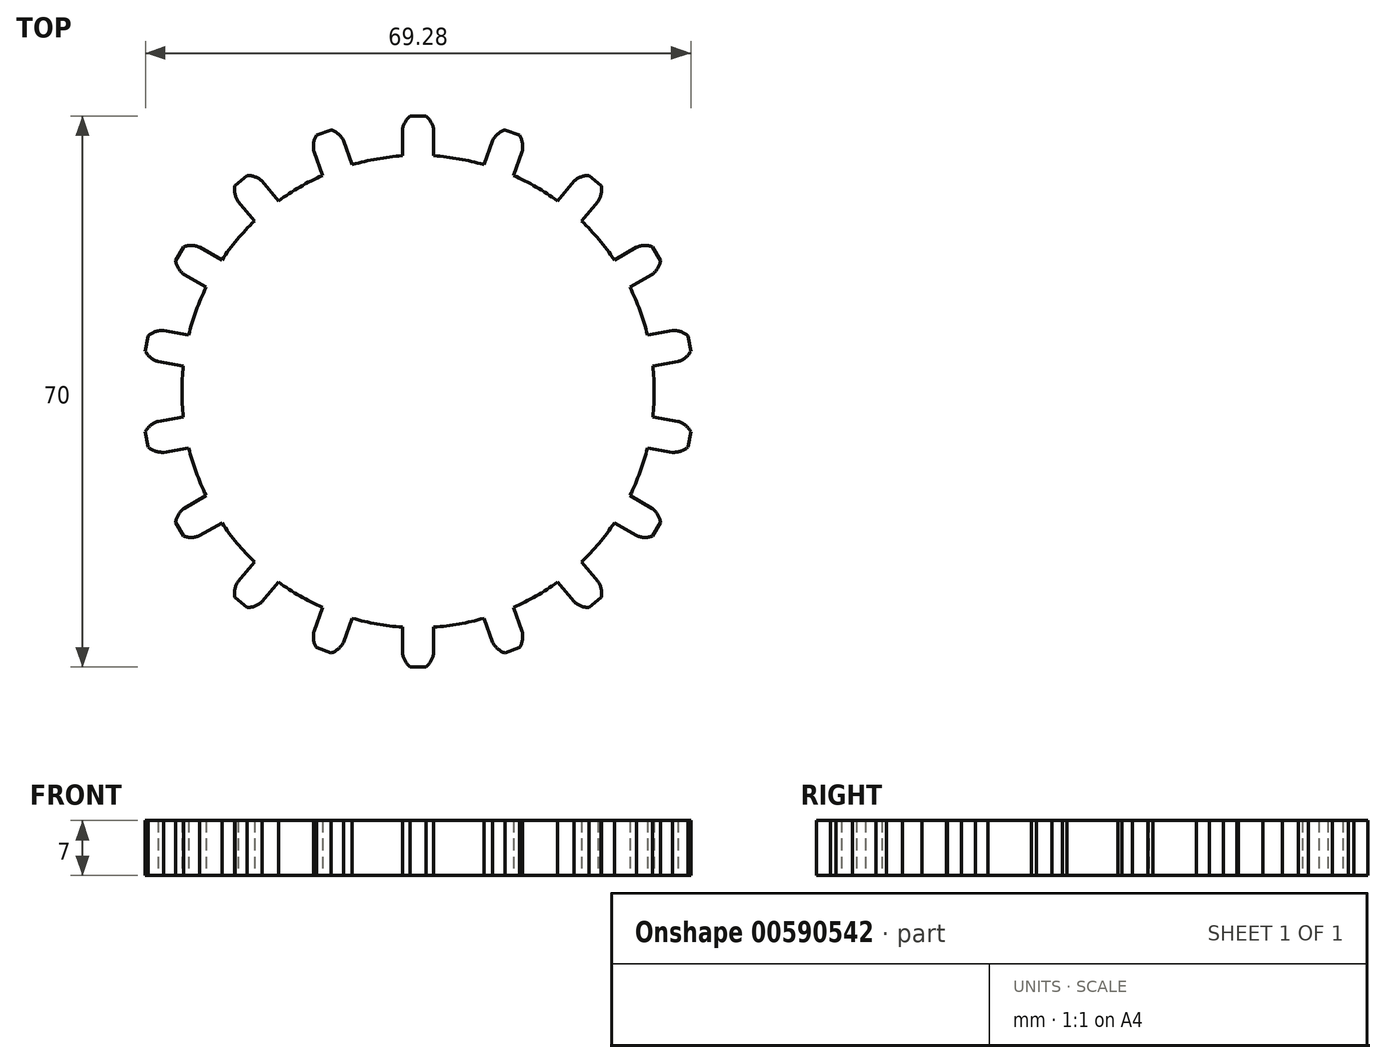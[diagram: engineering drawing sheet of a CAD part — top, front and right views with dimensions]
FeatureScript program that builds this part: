
annotation { "Feature Type Name" : "Feature", "Feature Type Description" : "" }
export const myFeature = defineFeature(function(context is Context, id is Id, definition is map)
    precondition{}
    {
        {
            var Q0;
            Q0=qCreatedBy(makeId("Top.planeOp"),FACE);
            var sketch = newSketch(context, id + "F0", { "sketchPlane" : qUnion([Q0])});
            skCircle(sketch, "E0", {"center": v(0, 0) * mm, "radius": 30 * mm});
            skLineSegment(sketch, "E1", {"start": v(0, 35) * mm, "end": v(1, 35) * mm});
            skLineSegment(sketch, "E2", {"start": v(2, 33.18) * mm, "end": v(2, 29.93) * mm});
            skPoint(sketch, "E3", {"position": v(1, 35) * mm});
            skArc(sketch, "E4", {"start": v(2, 32.47) * mm, "mid": v(1.82, 33.86) * mm, "end": v(1, 35) * mm});
            skPoint(sketch, "E5.MirrorCS.start.orphan", {"position": v(0, 35) * mm});
            skArc(sketch, "E6.MirrorCS", {"start": v(-2, 32.47) * mm, "mid": v(-1.82, 33.86) * mm, "end": v(-1, 35) * mm});
            skLineSegment(sketch, "E7.MirrorCS", {"start": v(-2, 33.18) * mm, "end": v(-2, 29.93) * mm});
            skLineSegment(sketch, "E8.MirrorCS", {"start": v(0, 35) * mm, "end": v(-1, 35) * mm});
            skLineSegment(sketch, "E9.1.0", {"start": v(-13.23, 30.5) * mm, "end": v(-12.12, 27.44) * mm});
            skLineSegment(sketch, "E9.1.1", {"start": v(-9.47, 31.86) * mm, "end": v(-8.36, 28.81) * mm});
            skPoint(sketch, "E9.1.2", {"position": v(-11.97, 32.89) * mm});
            skPoint(sketch, "E9.1.3", {"position": v(-11.03, 33.23) * mm});
            skArc(sketch, "E9.1.4", {"start": v(-12.98, 29.82) * mm, "mid": v(-13.3, 31.2) * mm, "end": v(-12.91, 32.55) * mm});
            skArc(sketch, "E9.1.5", {"start": v(-9.22, 31.2) * mm, "mid": v(-9.87, 32.44) * mm, "end": v(-11.03, 33.23) * mm});
            skLineSegment(sketch, "E9.1.6", {"start": v(-11.97, 32.89) * mm, "end": v(-12.91, 32.55) * mm});
            skLineSegment(sketch, "E9.1.7", {"start": v(-11.97, 32.89) * mm, "end": v(-11.03, 33.23) * mm});
            skLineSegment(sketch, "E9.2.0", {"start": v(-22.86, 24.13) * mm, "end": v(-20.77, 21.64) * mm});
            skLineSegment(sketch, "E9.2.1", {"start": v(-19.8, 26.7) * mm, "end": v(-17.7, 24.22) * mm});
            skPoint(sketch, "E9.2.2", {"position": v(-22.5, 26.81) * mm});
            skPoint(sketch, "E9.2.3", {"position": v(-21.73, 27.45) * mm});
            skArc(sketch, "E9.2.4", {"start": v(-22.4, 23.59) * mm, "mid": v(-23.16, 24.77) * mm, "end": v(-23.26, 26.17) * mm});
            skArc(sketch, "E9.2.5", {"start": v(-19.34, 26.16) * mm, "mid": v(-20.37, 27.11) * mm, "end": v(-21.73, 27.45) * mm});
            skLineSegment(sketch, "E9.2.6", {"start": v(-22.5, 26.81) * mm, "end": v(-23.26, 26.17) * mm});
            skLineSegment(sketch, "E9.2.7", {"start": v(-22.5, 26.81) * mm, "end": v(-21.73, 27.45) * mm});
            skLineSegment(sketch, "E9.3.0", {"start": v(-29.73, 14.86) * mm, "end": v(-26.92, 13.23) * mm});
            skLineSegment(sketch, "E9.3.1", {"start": v(-27.73, 18.32) * mm, "end": v(-24.92, 16.7) * mm});
            skPoint(sketch, "E9.3.2", {"position": v(-30.31, 17.5) * mm});
            skPoint(sketch, "E9.3.3", {"position": v(-29.81, 18.37) * mm});
            skArc(sketch, "E9.3.4", {"start": v(-29.12, 14.5) * mm, "mid": v(-30.24, 15.35) * mm, "end": v(-30.81, 16.63) * mm});
            skArc(sketch, "E9.3.5", {"start": v(-27.12, 17.97) * mm, "mid": v(-28.41, 18.51) * mm, "end": v(-29.81, 18.37) * mm});
            skLineSegment(sketch, "E9.3.6", {"start": v(-30.31, 17.5) * mm, "end": v(-30.81, 16.63) * mm});
            skLineSegment(sketch, "E9.3.7", {"start": v(-30.31, 17.5) * mm, "end": v(-29.81, 18.37) * mm});
            skLineSegment(sketch, "E9.4.0", {"start": v(-33.02, 3.8) * mm, "end": v(-29.83, 3.23) * mm});
            skLineSegment(sketch, "E9.4.1", {"start": v(-32.32, 7.73) * mm, "end": v(-29.13, 7.17) * mm});
            skPoint(sketch, "E9.4.2", {"position": v(-34.47, 6.08) * mm});
            skPoint(sketch, "E9.4.3", {"position": v(-34.3, 7.06) * mm});
            skArc(sketch, "E9.4.4", {"start": v(-32.32, 3.67) * mm, "mid": v(-33.66, 4.08) * mm, "end": v(-34.64, 5.1) * mm});
            skArc(sketch, "E9.4.5", {"start": v(-31.63, 7.6) * mm, "mid": v(-33.03, 7.68) * mm, "end": v(-34.3, 7.06) * mm});
            skLineSegment(sketch, "E9.4.6", {"start": v(-34.47, 6.08) * mm, "end": v(-34.64, 5.1) * mm});
            skLineSegment(sketch, "E9.4.7", {"start": v(-34.47, 6.08) * mm, "end": v(-34.3, 7.06) * mm});
            skLineSegment(sketch, "E9.5.0", {"start": v(-32.32, -7.73) * mm, "end": v(-29.13, -7.17) * mm});
            skLineSegment(sketch, "E9.5.1", {"start": v(-33.02, -3.8) * mm, "end": v(-29.83, -3.23) * mm});
            skPoint(sketch, "E9.5.2", {"position": v(-34.47, -6.08) * mm});
            skPoint(sketch, "E9.5.3", {"position": v(-34.64, -5.1) * mm});
            skArc(sketch, "E9.5.4", {"start": v(-31.63, -7.6) * mm, "mid": v(-33.03, -7.68) * mm, "end": v(-34.3, -7.06) * mm});
            skArc(sketch, "E9.5.5", {"start": v(-32.32, -3.67) * mm, "mid": v(-33.66, -4.08) * mm, "end": v(-34.64, -5.1) * mm});
            skLineSegment(sketch, "E9.5.6", {"start": v(-34.47, -6.08) * mm, "end": v(-34.3, -7.06) * mm});
            skLineSegment(sketch, "E9.5.7", {"start": v(-34.47, -6.08) * mm, "end": v(-34.64, -5.1) * mm});
            skLineSegment(sketch, "E9.6.0", {"start": v(-27.73, -18.32) * mm, "end": v(-24.92, -16.7) * mm});
            skLineSegment(sketch, "E9.6.1", {"start": v(-29.73, -14.86) * mm, "end": v(-26.92, -13.23) * mm});
            skPoint(sketch, "E9.6.2", {"position": v(-30.31, -17.5) * mm});
            skPoint(sketch, "E9.6.3", {"position": v(-30.81, -16.63) * mm});
            skArc(sketch, "E9.6.4", {"start": v(-27.12, -17.97) * mm, "mid": v(-28.41, -18.51) * mm, "end": v(-29.81, -18.37) * mm});
            skArc(sketch, "E9.6.5", {"start": v(-29.12, -14.5) * mm, "mid": v(-30.24, -15.35) * mm, "end": v(-30.81, -16.63) * mm});
            skLineSegment(sketch, "E9.6.6", {"start": v(-30.31, -17.5) * mm, "end": v(-29.81, -18.37) * mm});
            skLineSegment(sketch, "E9.6.7", {"start": v(-30.31, -17.5) * mm, "end": v(-30.81, -16.63) * mm});
            skLineSegment(sketch, "E9.7.0", {"start": v(-19.8, -26.7) * mm, "end": v(-17.7, -24.22) * mm});
            skLineSegment(sketch, "E9.7.1", {"start": v(-22.86, -24.13) * mm, "end": v(-20.77, -21.64) * mm});
            skPoint(sketch, "E9.7.2", {"position": v(-22.5, -26.81) * mm});
            skPoint(sketch, "E9.7.3", {"position": v(-23.26, -26.17) * mm});
            skArc(sketch, "E9.7.4", {"start": v(-19.34, -26.16) * mm, "mid": v(-20.37, -27.11) * mm, "end": v(-21.73, -27.45) * mm});
            skArc(sketch, "E9.7.5", {"start": v(-22.4, -23.59) * mm, "mid": v(-23.16, -24.77) * mm, "end": v(-23.26, -26.17) * mm});
            skLineSegment(sketch, "E9.7.6", {"start": v(-22.5, -26.81) * mm, "end": v(-21.73, -27.45) * mm});
            skLineSegment(sketch, "E9.7.7", {"start": v(-22.5, -26.81) * mm, "end": v(-23.26, -26.17) * mm});
            skLineSegment(sketch, "E9.8.0", {"start": v(-9.47, -31.86) * mm, "end": v(-8.36, -28.81) * mm});
            skLineSegment(sketch, "E9.8.1", {"start": v(-13.23, -30.5) * mm, "end": v(-12.12, -27.44) * mm});
            skPoint(sketch, "E9.8.2", {"position": v(-11.97, -32.89) * mm});
            skPoint(sketch, "E9.8.3", {"position": v(-12.91, -32.55) * mm});
            skArc(sketch, "E9.8.4", {"start": v(-9.22, -31.2) * mm, "mid": v(-9.87, -32.44) * mm, "end": v(-11.03, -33.23) * mm});
            skArc(sketch, "E9.8.5", {"start": v(-12.98, -29.82) * mm, "mid": v(-13.3, -31.2) * mm, "end": v(-12.91, -32.55) * mm});
            skLineSegment(sketch, "E9.8.6", {"start": v(-11.97, -32.89) * mm, "end": v(-11.03, -33.23) * mm});
            skLineSegment(sketch, "E9.8.7", {"start": v(-11.97, -32.89) * mm, "end": v(-12.91, -32.55) * mm});
            skLineSegment(sketch, "E9.9.0", {"start": v(2, -33.18) * mm, "end": v(2, -29.93) * mm});
            skLineSegment(sketch, "E9.9.1", {"start": v(-2, -33.18) * mm, "end": v(-2, -29.93) * mm});
            skPoint(sketch, "E9.9.2", {"position": v(0, -35) * mm});
            skPoint(sketch, "E9.9.3", {"position": v(-1, -35) * mm});
            skArc(sketch, "E9.9.4", {"start": v(2, -32.47) * mm, "mid": v(1.82, -33.86) * mm, "end": v(1, -35) * mm});
            skArc(sketch, "E9.9.5", {"start": v(-2, -32.47) * mm, "mid": v(-1.82, -33.86) * mm, "end": v(-1, -35) * mm});
            skLineSegment(sketch, "E9.9.6", {"start": v(0, -35) * mm, "end": v(1, -35) * mm});
            skLineSegment(sketch, "E9.9.7", {"start": v(0, -35) * mm, "end": v(-1, -35) * mm});
            skLineSegment(sketch, "E9.10.0", {"start": v(13.23, -30.5) * mm, "end": v(12.12, -27.44) * mm});
            skLineSegment(sketch, "E9.10.1", {"start": v(9.47, -31.86) * mm, "end": v(8.36, -28.81) * mm});
            skPoint(sketch, "E9.10.2", {"position": v(11.97, -32.89) * mm});
            skPoint(sketch, "E9.10.3", {"position": v(11.03, -33.23) * mm});
            skArc(sketch, "E9.10.4", {"start": v(12.98, -29.82) * mm, "mid": v(13.3, -31.2) * mm, "end": v(12.91, -32.55) * mm});
            skArc(sketch, "E9.10.5", {"start": v(9.22, -31.2) * mm, "mid": v(9.87, -32.44) * mm, "end": v(11.03, -33.23) * mm});
            skLineSegment(sketch, "E9.10.6", {"start": v(11.97, -32.89) * mm, "end": v(12.91, -32.55) * mm});
            skLineSegment(sketch, "E9.10.7", {"start": v(11.97, -32.89) * mm, "end": v(11.03, -33.23) * mm});
            skLineSegment(sketch, "E9.11.0", {"start": v(22.86, -24.13) * mm, "end": v(20.77, -21.64) * mm});
            skLineSegment(sketch, "E9.11.1", {"start": v(19.8, -26.7) * mm, "end": v(17.7, -24.22) * mm});
            skPoint(sketch, "E9.11.2", {"position": v(22.5, -26.81) * mm});
            skPoint(sketch, "E9.11.3", {"position": v(21.73, -27.45) * mm});
            skArc(sketch, "E9.11.4", {"start": v(22.4, -23.59) * mm, "mid": v(23.16, -24.77) * mm, "end": v(23.26, -26.17) * mm});
            skArc(sketch, "E9.11.5", {"start": v(19.34, -26.16) * mm, "mid": v(20.37, -27.11) * mm, "end": v(21.73, -27.45) * mm});
            skLineSegment(sketch, "E9.11.6", {"start": v(22.5, -26.81) * mm, "end": v(23.26, -26.17) * mm});
            skLineSegment(sketch, "E9.11.7", {"start": v(22.5, -26.81) * mm, "end": v(21.73, -27.45) * mm});
            skLineSegment(sketch, "E9.12.0", {"start": v(29.73, -14.86) * mm, "end": v(26.92, -13.23) * mm});
            skLineSegment(sketch, "E9.12.1", {"start": v(27.73, -18.32) * mm, "end": v(24.92, -16.7) * mm});
            skPoint(sketch, "E9.12.2", {"position": v(30.31, -17.5) * mm});
            skPoint(sketch, "E9.12.3", {"position": v(29.81, -18.37) * mm});
            skArc(sketch, "E9.12.4", {"start": v(29.12, -14.5) * mm, "mid": v(30.24, -15.35) * mm, "end": v(30.81, -16.63) * mm});
            skArc(sketch, "E9.12.5", {"start": v(27.12, -17.97) * mm, "mid": v(28.41, -18.51) * mm, "end": v(29.81, -18.37) * mm});
            skLineSegment(sketch, "E9.12.6", {"start": v(30.31, -17.5) * mm, "end": v(30.81, -16.63) * mm});
            skLineSegment(sketch, "E9.12.7", {"start": v(30.31, -17.5) * mm, "end": v(29.81, -18.37) * mm});
            skLineSegment(sketch, "E9.13.0", {"start": v(33.02, -3.8) * mm, "end": v(29.83, -3.23) * mm});
            skLineSegment(sketch, "E9.13.1", {"start": v(32.32, -7.73) * mm, "end": v(29.13, -7.17) * mm});
            skPoint(sketch, "E9.13.2", {"position": v(34.47, -6.08) * mm});
            skPoint(sketch, "E9.13.3", {"position": v(34.3, -7.06) * mm});
            skArc(sketch, "E9.13.4", {"start": v(32.32, -3.67) * mm, "mid": v(33.66, -4.08) * mm, "end": v(34.64, -5.1) * mm});
            skArc(sketch, "E9.13.5", {"start": v(31.63, -7.6) * mm, "mid": v(33.03, -7.68) * mm, "end": v(34.3, -7.06) * mm});
            skLineSegment(sketch, "E9.13.6", {"start": v(34.47, -6.08) * mm, "end": v(34.64, -5.1) * mm});
            skLineSegment(sketch, "E9.13.7", {"start": v(34.47, -6.08) * mm, "end": v(34.3, -7.06) * mm});
            skLineSegment(sketch, "E9.14.0", {"start": v(32.32, 7.73) * mm, "end": v(29.13, 7.17) * mm});
            skLineSegment(sketch, "E9.14.1", {"start": v(33.02, 3.8) * mm, "end": v(29.83, 3.23) * mm});
            skPoint(sketch, "E9.14.2", {"position": v(34.47, 6.08) * mm});
            skPoint(sketch, "E9.14.3", {"position": v(34.64, 5.1) * mm});
            skArc(sketch, "E9.14.4", {"start": v(31.63, 7.6) * mm, "mid": v(33.03, 7.68) * mm, "end": v(34.3, 7.06) * mm});
            skArc(sketch, "E9.14.5", {"start": v(32.32, 3.67) * mm, "mid": v(33.66, 4.08) * mm, "end": v(34.64, 5.1) * mm});
            skLineSegment(sketch, "E9.14.6", {"start": v(34.47, 6.08) * mm, "end": v(34.3, 7.06) * mm});
            skLineSegment(sketch, "E9.14.7", {"start": v(34.47, 6.08) * mm, "end": v(34.64, 5.1) * mm});
            skLineSegment(sketch, "E9.15.0", {"start": v(27.73, 18.32) * mm, "end": v(24.92, 16.7) * mm});
            skLineSegment(sketch, "E9.15.1", {"start": v(29.73, 14.86) * mm, "end": v(26.92, 13.23) * mm});
            skPoint(sketch, "E9.15.2", {"position": v(30.31, 17.5) * mm});
            skPoint(sketch, "E9.15.3", {"position": v(30.81, 16.63) * mm});
            skArc(sketch, "E9.15.4", {"start": v(27.12, 17.97) * mm, "mid": v(28.41, 18.51) * mm, "end": v(29.81, 18.37) * mm});
            skArc(sketch, "E9.15.5", {"start": v(29.12, 14.5) * mm, "mid": v(30.24, 15.35) * mm, "end": v(30.81, 16.63) * mm});
            skLineSegment(sketch, "E9.15.6", {"start": v(30.31, 17.5) * mm, "end": v(29.81, 18.37) * mm});
            skLineSegment(sketch, "E9.15.7", {"start": v(30.31, 17.5) * mm, "end": v(30.81, 16.63) * mm});
            skLineSegment(sketch, "E9.16.0", {"start": v(19.8, 26.7) * mm, "end": v(17.7, 24.22) * mm});
            skLineSegment(sketch, "E9.16.1", {"start": v(22.86, 24.13) * mm, "end": v(20.77, 21.64) * mm});
            skPoint(sketch, "E9.16.2", {"position": v(22.5, 26.81) * mm});
            skPoint(sketch, "E9.16.3", {"position": v(23.26, 26.17) * mm});
            skArc(sketch, "E9.16.4", {"start": v(19.34, 26.16) * mm, "mid": v(20.37, 27.11) * mm, "end": v(21.73, 27.45) * mm});
            skArc(sketch, "E9.16.5", {"start": v(22.4, 23.59) * mm, "mid": v(23.16, 24.77) * mm, "end": v(23.26, 26.17) * mm});
            skLineSegment(sketch, "E9.16.6", {"start": v(22.5, 26.81) * mm, "end": v(21.73, 27.45) * mm});
            skLineSegment(sketch, "E9.16.7", {"start": v(22.5, 26.81) * mm, "end": v(23.26, 26.17) * mm});
            skLineSegment(sketch, "E9.17.0", {"start": v(9.47, 31.86) * mm, "end": v(8.36, 28.81) * mm});
            skLineSegment(sketch, "E9.17.1", {"start": v(13.23, 30.5) * mm, "end": v(12.12, 27.44) * mm});
            skPoint(sketch, "E9.17.2", {"position": v(11.97, 32.89) * mm});
            skPoint(sketch, "E9.17.3", {"position": v(12.91, 32.55) * mm});
            skArc(sketch, "E9.17.4", {"start": v(9.22, 31.2) * mm, "mid": v(9.87, 32.44) * mm, "end": v(11.03, 33.23) * mm});
            skArc(sketch, "E9.17.5", {"start": v(12.98, 29.82) * mm, "mid": v(13.3, 31.2) * mm, "end": v(12.91, 32.55) * mm});
            skLineSegment(sketch, "E9.17.6", {"start": v(11.97, 32.89) * mm, "end": v(11.03, 33.23) * mm});
            skLineSegment(sketch, "E9.17.7", {"start": v(11.97, 32.89) * mm, "end": v(12.91, 32.55) * mm});
            skSolve(sketch);
        }
        {
            var Q0;
            {var subQ0=sQuery(id+"F0.wireOp",EDGE,"E0");var subQ17=makeQuery(id+"F0.imprint","INTERSECT",VERTEX,{"derivedFrom":[subQ0,sQuery(id+"F0.wireOp",EDGE,"E9.14.0")]});Q0=makeQuery(id+"F0.imprint","IMPRINT",FACE,{"disambiguationData":[TD([[makeQuery(id+"F0.imprint","IMPRINT",EDGE,{"disambiguationData":[TD([[subQ17,1.0]])],"derivedFrom":subQ0}),1.0]])]});}
            var Q1;
            {var subQ11=sQuery(id+"F0.wireOp",EDGE,"E9.1.6");Q1=makeQuery(id+"F0.imprint","IMPRINT",FACE,{"disambiguationData":[TD([[makeQuery(id+"F0.imprint","IMPRINT",EDGE,{"derivedFrom":subQ11}),1.0]])]});}
            var Q2;
            {var subQ11=sQuery(id+"F0.wireOp",EDGE,"E9.2.6");Q2=makeQuery(id+"F0.imprint","IMPRINT",FACE,{"disambiguationData":[TD([[makeQuery(id+"F0.imprint","IMPRINT",EDGE,{"derivedFrom":subQ11}),1.0]])]});}
            var Q3;
            {var subQ11=sQuery(id+"F0.wireOp",EDGE,"E9.3.6");Q3=makeQuery(id+"F0.imprint","IMPRINT",FACE,{"disambiguationData":[TD([[makeQuery(id+"F0.imprint","IMPRINT",EDGE,{"derivedFrom":subQ11}),1.0]])]});}
            var Q4;
            {var subQ11=sQuery(id+"F0.wireOp",EDGE,"E9.4.6");Q4=makeQuery(id+"F0.imprint","IMPRINT",FACE,{"disambiguationData":[TD([[makeQuery(id+"F0.imprint","IMPRINT",EDGE,{"derivedFrom":subQ11}),1.0]])]});}
            var Q5;
            {var subQ12=sQuery(id+"F0.wireOp",EDGE,"E9.5.6");Q5=makeQuery(id+"F0.imprint","IMPRINT",FACE,{"disambiguationData":[TD([[makeQuery(id+"F0.imprint","IMPRINT",EDGE,{"derivedFrom":subQ12}),1.0]])]});}
            var Q6;
            {var subQ11=sQuery(id+"F0.wireOp",EDGE,"E9.6.6");Q6=makeQuery(id+"F0.imprint","IMPRINT",FACE,{"disambiguationData":[TD([[makeQuery(id+"F0.imprint","IMPRINT",EDGE,{"derivedFrom":subQ11}),1.0]])]});}
            var Q7;
            {var subQ11=sQuery(id+"F0.wireOp",EDGE,"E9.7.6");Q7=makeQuery(id+"F0.imprint","IMPRINT",FACE,{"disambiguationData":[TD([[makeQuery(id+"F0.imprint","IMPRINT",EDGE,{"derivedFrom":subQ11}),1.0]])]});}
            var Q8;
            {var subQ12=sQuery(id+"F0.wireOp",EDGE,"E9.8.6");Q8=makeQuery(id+"F0.imprint","IMPRINT",FACE,{"disambiguationData":[TD([[makeQuery(id+"F0.imprint","IMPRINT",EDGE,{"derivedFrom":subQ12}),1.0]])]});}
            var Q9;
            {var subQ11=sQuery(id+"F0.wireOp",EDGE,"E9.9.6");Q9=makeQuery(id+"F0.imprint","IMPRINT",FACE,{"disambiguationData":[TD([[makeQuery(id+"F0.imprint","IMPRINT",EDGE,{"derivedFrom":subQ11}),1.0]])]});}
            var Q10;
            {var subQ11=sQuery(id+"F0.wireOp",EDGE,"E9.10.6");Q10=makeQuery(id+"F0.imprint","IMPRINT",FACE,{"disambiguationData":[TD([[makeQuery(id+"F0.imprint","IMPRINT",EDGE,{"derivedFrom":subQ11}),1.0]])]});}
            var Q11;
            {var subQ11=sQuery(id+"F0.wireOp",EDGE,"E9.11.6");Q11=makeQuery(id+"F0.imprint","IMPRINT",FACE,{"disambiguationData":[TD([[makeQuery(id+"F0.imprint","IMPRINT",EDGE,{"derivedFrom":subQ11}),1.0]])]});}
            var Q12;
            {var subQ11=sQuery(id+"F0.wireOp",EDGE,"E9.12.6");Q12=makeQuery(id+"F0.imprint","IMPRINT",FACE,{"disambiguationData":[TD([[makeQuery(id+"F0.imprint","IMPRINT",EDGE,{"derivedFrom":subQ11}),1.0]])]});}
            var Q13;
            {var subQ11=sQuery(id+"F0.wireOp",EDGE,"E9.13.6");Q13=makeQuery(id+"F0.imprint","IMPRINT",FACE,{"disambiguationData":[TD([[makeQuery(id+"F0.imprint","IMPRINT",EDGE,{"derivedFrom":subQ11}),1.0]])]});}
            var Q14;
            {var subQ11=sQuery(id+"F0.wireOp",EDGE,"E9.14.6");Q14=makeQuery(id+"F0.imprint","IMPRINT",FACE,{"disambiguationData":[TD([[makeQuery(id+"F0.imprint","IMPRINT",EDGE,{"derivedFrom":subQ11}),1.0]])]});}
            var Q15;
            {var subQ11=sQuery(id+"F0.wireOp",EDGE,"E9.15.6");Q15=makeQuery(id+"F0.imprint","IMPRINT",FACE,{"disambiguationData":[TD([[makeQuery(id+"F0.imprint","IMPRINT",EDGE,{"derivedFrom":subQ11}),1.0]])]});}
            var Q16;
            {var subQ11=sQuery(id+"F0.wireOp",EDGE,"E9.16.6");Q16=makeQuery(id+"F0.imprint","IMPRINT",FACE,{"disambiguationData":[TD([[makeQuery(id+"F0.imprint","IMPRINT",EDGE,{"derivedFrom":subQ11}),1.0]])]});}
            var Q17;
            {var subQ12=sQuery(id+"F0.wireOp",EDGE,"E9.17.6");Q17=makeQuery(id+"F0.imprint","IMPRINT",FACE,{"disambiguationData":[TD([[makeQuery(id+"F0.imprint","IMPRINT",EDGE,{"derivedFrom":subQ12}),1.0]])]});}
            var Q18;
            {var subQ4=sQuery(id+"F0.wireOp",EDGE,"E1");Q18=makeQuery(id+"F0.imprint","IMPRINT",FACE,{"disambiguationData":[TD([[makeQuery(id+"F0.imprint","IMPRINT",EDGE,{"derivedFrom":subQ4}),-1.0]])]});}
            extrude(context, id + "F1", {"entities" : qUnion([Q0, Q1, Q2, Q3, Q4, Q5, Q6, Q7, Q8, Q9, Q10, Q11, Q12, Q13, Q14, Q15, Q16, Q17, Q18]), "depth" : 7 * mm, "offsetDistance" : 25 * mm});
        }
    });
